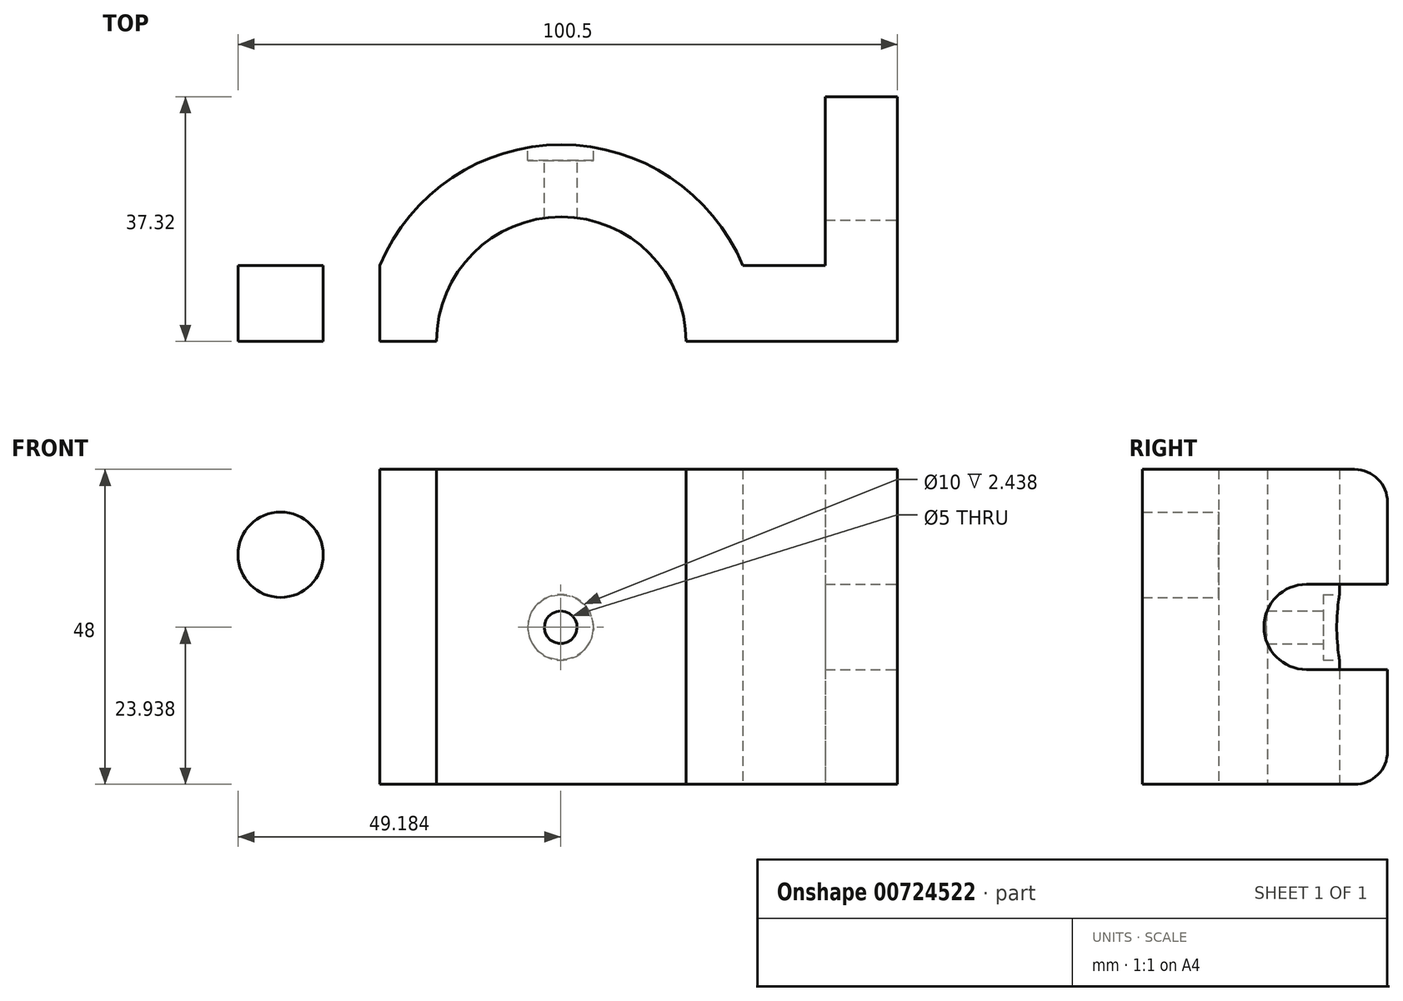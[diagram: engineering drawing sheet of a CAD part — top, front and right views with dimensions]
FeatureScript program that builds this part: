
annotation { "Feature Type Name" : "Feature", "Feature Type Description" : "" }
export const myFeature = defineFeature(function(context is Context, id is Id, definition is map)
    precondition{}
    {
        {
            var Q0;
            Q0=qCreatedBy(makeId("Top.planeOp"),FACE);
            var sketch = newSketch(context, id + "F0", { "sketchPlane" : qUnion([Q0])});
            skLineSegment(sketch, "E0", {"start": v(-36.77, 12.22) * mm, "end": v(-36.77, 0) * mm});
            skLineSegment(sketch, "E1", {"start": v(-36.77, 0) * mm, "end": v(0, 0) * mm});
            skArc(sketch, "E2", {"start": v(0, 0) * mm, "mid": v(19, 19) * mm, "end": v(38, 0) * mm});
            skLineSegment(sketch, "E3", {"start": v(-8.68, 11.57) * mm, "end": v(-36.77, 11.57) * mm});
            skPoint(sketch, "E3.endSnap0", {"position": v(-36.77, 6.1) * mm});
            skArc(sketch, "E4", {"start": v(-8.68, 11.57) * mm, "mid": v(19, 30) * mm, "end": v(46.68, 11.57) * mm});
            skLineSegment(sketch, "E5", {"start": v(46.68, 11.57) * mm, "end": v(59.23, 11.57) * mm});
            skLineSegment(sketch, "E6", {"start": v(38, 0) * mm, "end": v(70.23, 0) * mm});
            skLineSegment(sketch, "E7", {"start": v(59.23, 11.57) * mm, "end": v(59.23, 37.32) * mm});
            skLineSegment(sketch, "E8", {"start": v(70.23, 37.32) * mm, "end": v(70.23, 0) * mm});
            skLineSegment(sketch, "E9", {"start": v(59.23, 37.32) * mm, "end": v(70.23, 37.32) * mm});
            skLineSegment(sketch, "E10", {"start": v(19, 0) * mm, "end": v(19, 30) * mm, "construction": true});
            skPoint(sketch, "E11", {"position": v(19, 30) * mm});
            skSolve(sketch);
        }
        {
            var Q0;
            {var subQ1=sQuery(id+"F0.wireOp",EDGE,"E1");Q0=makeQuery(id+"F0.imprint","IMPRINT",FACE,{"disambiguationData":[TD([[makeQuery(id+"F0.imprint","IMPRINT",EDGE,{"derivedFrom":subQ1}),1.0]])]});}
            extrude(context, id + "F1", {"entities" : qUnion([Q0]), "depth" : 48 * mm});
        }
        {
            var Q0;
            Q0=makeQuery(id+"F1.opExtrude","CAP_EDGE",EDGE,{"disambiguationData":[OSD([sQuery(id+"F0.wireOp",EDGE,"E9")])],"isStart":false});
            var Q1;
            Q1=makeQuery(id+"F1.opExtrude","CAP_EDGE",EDGE,{"disambiguationData":[OSD([sQuery(id+"F0.wireOp",EDGE,"E9")])],"isStart":true});
            fillet(context, id + "F2", {"entities" : qUnion([Q0, Q1]), "radius" : 5 * mm, "tangentPropagation" : true, "allowEdgeOverflow" : false});
        }
        {
            var Q0;
            Q0=makeQuery(id+"F1.opExtrude","SWEPT_FACE",FACE,{"disambiguationData":[OSD([sQuery(id+"F0.wireOp",EDGE,"E8")])]});
            var sketch = newSketch(context, id + "F3", { "sketchPlane" : qUnion([Q0])});
            skLineSegment(sketch, "E12", {"start": v(37.32, 30.5) * mm, "end": v(25, 30.5) * mm});
            skLineSegment(sketch, "E13", {"start": v(37.32, 17.5) * mm, "end": v(25, 17.5) * mm});
            skArc(sketch, "E14", {"start": v(25, 17.5) * mm, "mid": v(18.5, 24) * mm, "end": v(25, 30.5) * mm});
            skArc(sketch, "E15", {"start": v(25, 30.5) * mm, "mid": v(18.5, 24) * mm, "end": v(25, 17.5) * mm});
            skLineSegment(sketch, "E16", {"start": v(37.32, 24) * mm, "end": v(0, 24) * mm, "construction": true});
            skLineSegment(sketch, "E17", {"start": v(0, 48) * mm, "end": v(0, 0) * mm});
            skSolve(sketch);
        }
        {
            var Q0;
            Q0=qSketchRegion(id+"F3",true);
            var Q1;
            {var subQ0=sQuery(id+"F3.wireOp",EDGE,"E12");Q1=makeQuery(id+"F3.imprint","IMPRINT",FACE,{"disambiguationData":[TD([[makeQuery(id+"F3.imprint","IMPRINT",EDGE,{"derivedFrom":subQ0}),1.0]])]});}
            extrude(context, id + "F4", {"entities" : qUnion([Q0, Q1]), "operationType" : NewBodyOperationType.REMOVE, "oppositeDirection" : true, "depth" : 11 * mm});
        }
        {
            var Q0;
            Q0=makeQuery(id+"F1.opExtrude","CAP_EDGE",EDGE,{"disambiguationData":[OSD([sQuery(id+"F0.wireOp",EDGE,"E0")])],"isStart":false});
            var Q1;
            Q1=makeQuery(id+"F1.opExtrude","CAP_EDGE",EDGE,{"disambiguationData":[OSD([sQuery(id+"F0.wireOp",EDGE,"E0")])],"isStart":true});
            fillet(context, id + "F5", {"entities" : qUnion([Q0, Q1]), "radius" : 13 * mm, "tangentPropagation" : true, "allowEdgeOverflow" : false});
        }
        {
            var Q0;
            Q0=makeQuery(id+"F1.opExtrude","SWEPT_FACE",FACE,{"disambiguationData":[OSD([sQuery(id+"F0.wireOp",EDGE,"E3")])]});
            var sketch = newSketch(context, id + "F6", { "sketchPlane" : qUnion([Q0])});
            skCircle(sketch, "E18", {"center": v(23.77, 13) * mm, "radius": 6.5 * mm});
            skLineSegment(sketch, "E19", {"start": v(36.77, 24) * mm, "end": v(8.68, 24) * mm, "construction": true});
            skCircle(sketch, "E20.MirrorC", {"center": v(23.77, 35) * mm, "radius": 6.5 * mm});
            skSolve(sketch);
        }
        {
            var Q0;
            Q0=makeQuery(id+"F6.imprint","IMPRINT",FACE,{"disambiguationData":[TD([[makeQuery(id+"F6.imprint","IMPRINT",EDGE,{"derivedFrom":sQuery(id+"F6.wireOp",EDGE,"E18")}),1.0]])]});
            var Q1;
            Q1=makeQuery(id+"F6.imprint","IMPRINT",FACE,{"disambiguationData":[TD([[makeQuery(id+"F6.imprint","IMPRINT",EDGE,{"derivedFrom":sQuery(id+"F6.wireOp",EDGE,"E20.MirrorC")}),-1.0]])]});
            extrude(context, id + "F7", {"entities" : qUnion([Q0, Q1]), "operationType" : NewBodyOperationType.REMOVE, "oppositeDirection" : true, "depth" : 25 * mm});
        }
        {
            var Q0;
            Q0=qCreatedBy(makeId("Front.planeOp"),FACE);
            cPlane(context, id + "F8", {"entities" : qUnion([Q0]), "cplaneType" : CPlaneType.OFFSET, "offset" : 30 * mm, "oppositeDirection" : true, "width" : 150 * mm, "height" : 150 * mm});
        }
        {
            var Q0;
            Q0=qCreatedBy(id+"F8.planeOp",FACE);
            var sketch = newSketch(context, id + "F9", { "sketchPlane" : qUnion([Q0])});
            skLineSegment(sketch, "E21", {"start": v(18.91, 23.94) * mm, "end": v(18.91, 0) * mm});
            skLineSegment(sketch, "E22", {"start": v(18.91, 0) * mm, "end": v(18.91, 23.94) * mm});
            skLineSegment(sketch, "E23", {"start": v(18.91, 23.94) * mm, "end": v(18.91, 48.1) * mm});
            skPoint(sketch, "E24", {"position": v(18.91, 23.94) * mm});
            skSolve(sketch);
        }
        {
            var Q0;
            Q0=sQuery(id+"F9.wireOp",VERTEX,"E24");
            var Q1;
            Q1=makeQuery(id+"F1.opExtrude","SWEPT_BODY",BODY,{"disambiguationData":[OSD([sQuery(id+"F0.wireOp",EDGE,"E0"),sQuery(id+"F0.wireOp",EDGE,"E1"),sQuery(id+"F0.wireOp",EDGE,"E2"),sQuery(id+"F0.wireOp",EDGE,"E3"),sQuery(id+"F0.wireOp",EDGE,"E4"),sQuery(id+"F0.wireOp",EDGE,"E5"),sQuery(id+"F0.wireOp",EDGE,"E6"),sQuery(id+"F0.wireOp",EDGE,"E7"),sQuery(id+"F0.wireOp",EDGE,"E8"),sQuery(id+"F0.wireOp",EDGE,"E9")])]});
            hole(context, id + "F10", {"style" : HoleStyle.C_BORE, "endStyle" : HoleEndStyle.THROUGH, "oppositeDirection" : true, "holeDiameter" : 5 * mm, "cBoreDiameter" : 10 * mm, "cBoreDepth" : 2 * mm, "tappedDepth" : 12 * mm, "tapClearance" : 3, "locations" : qUnion([Q0]), "scope" : qUnion([Q1])});
        }
    });
